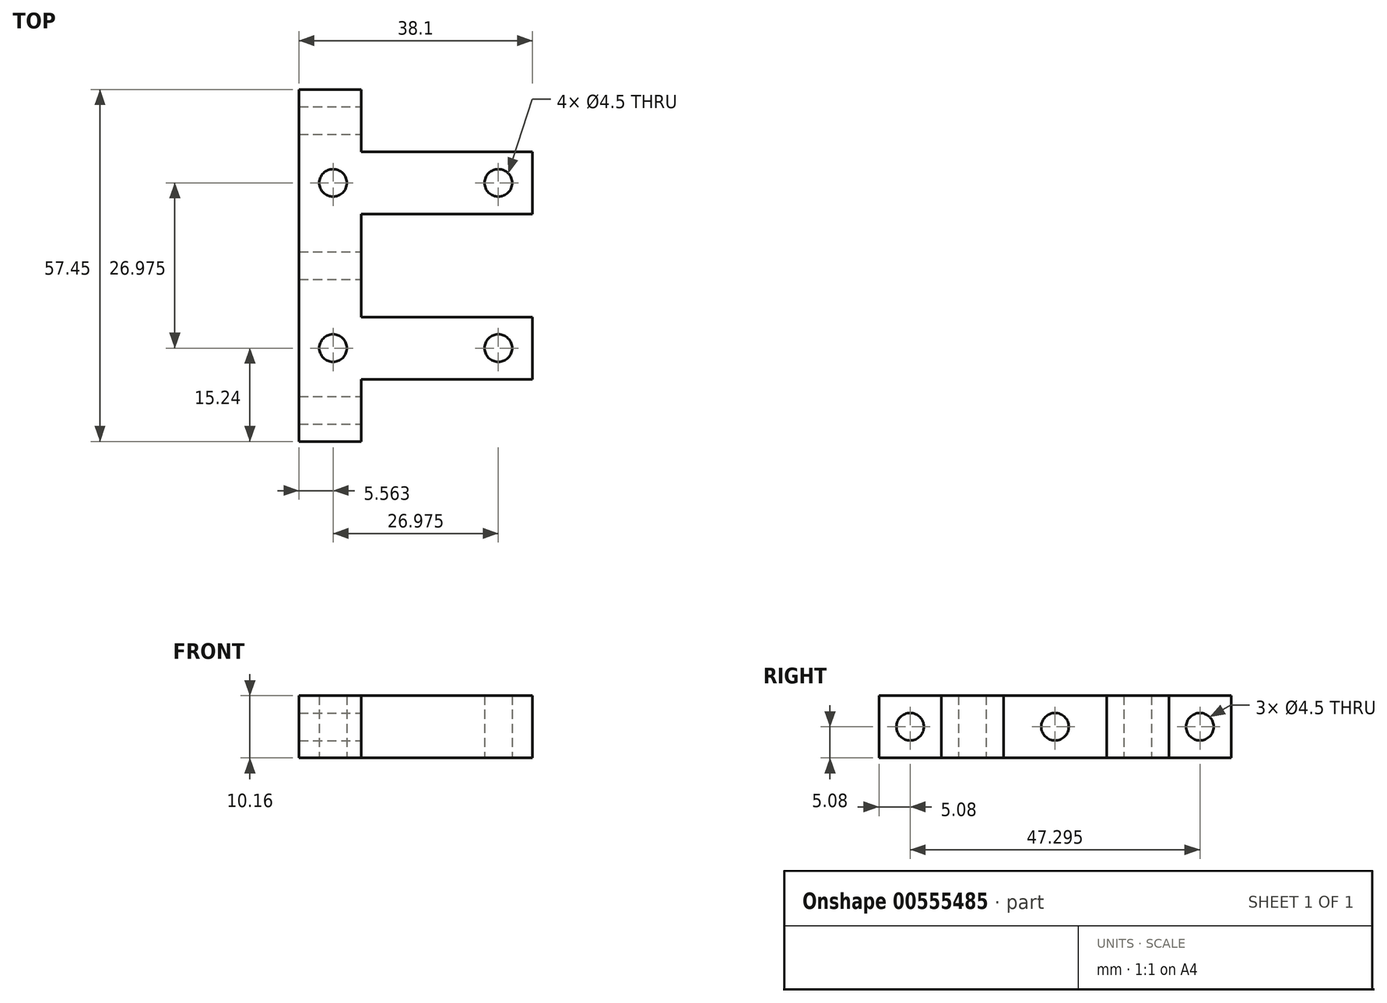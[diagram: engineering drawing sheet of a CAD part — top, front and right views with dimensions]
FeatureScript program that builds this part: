
annotation { "Feature Type Name" : "Feature", "Feature Type Description" : "" }
export const myFeature = defineFeature(function(context is Context, id is Id, definition is map)
    precondition{}
    {
        {
            var Q0;
            Q0=qCreatedBy(makeId("Top.planeOp"),FACE);
            var sketch = newSketch(context, id + "F0", { "sketchPlane" : qUnion([Q0])});
            skLineSegment(sketch, "E0.top", {"start": v(-19.05, -5.08) * mm, "end": v(19.05, -5.08) * mm});
            skPoint(sketch, "E0.middle", {"position": v(0, 0) * mm});
            skLineSegment(sketch, "E1", {"start": v(0, -30.1) * mm, "end": v(0, 45.98) * mm, "construction": true});
            skPoint(sketch, "E2", {"position": v(0, -5.08) * mm});
            skLineSegment(sketch, "E3", {"start": v(19.05, -5.08) * mm, "end": v(19.05, 5.08) * mm});
            skPoint(sketch, "E4", {"position": v(19.05, 0) * mm});
            skLineSegment(sketch, "E5", {"start": v(19.05, 0) * mm, "end": v(-19.05, 0) * mm, "construction": true});
            skPoint(sketch, "E6", {"position": v(-13.49, 0) * mm});
            skPoint(sketch, "E7", {"position": v(13.49, 0) * mm});
            skLineSegment(sketch, "E8", {"start": v(-19.05, -5.08) * mm, "end": v(-19.05, 32.05) * mm});
            skLineSegment(sketch, "E9", {"start": v(19.05, 5.08) * mm, "end": v(-8.89, 5.08) * mm});
            skLineSegment(sketch, "E10", {"start": v(-13.49, -5.08) * mm, "end": v(-13.49, 32.61) * mm, "construction": true});
            skPoint(sketch, "E11", {"position": v(-13.49, 26.97) * mm});
            skLineSegment(sketch, "E12", {"start": v(-19.05, 32.05) * mm, "end": v(19.05, 32.05) * mm});
            skLineSegment(sketch, "E13", {"start": v(-13.49, 26.97) * mm, "end": v(18.99, 26.97) * mm, "construction": true});
            skLineSegment(sketch, "E14", {"start": v(19.05, 32.05) * mm, "end": v(19.05, 21.9) * mm});
            skLineSegment(sketch, "E15", {"start": v(19.05, 21.9) * mm, "end": v(-8.9, 21.9) * mm});
            skLineSegment(sketch, "E16", {"start": v(-8.9, 21.9) * mm, "end": v(-8.89, 5.08) * mm});
            skPoint(sketch, "E17", {"position": v(13.49, 26.97) * mm});
            skLineSegment(sketch, "E18", {"start": v(-8.89, 5.08) * mm, "end": v(-8.89, -15.24) * mm});
            skLineSegment(sketch, "E19", {"start": v(-8.89, -15.24) * mm, "end": v(-19.05, -15.24) * mm});
            skLineSegment(sketch, "E20", {"start": v(-19.05, -15.24) * mm, "end": v(-19.05, -5.08) * mm});
            skLineSegment(sketch, "E21", {"start": v(-8.9, 21.9) * mm, "end": v(-8.9, 42.21) * mm});
            skLineSegment(sketch, "E22", {"start": v(-8.9, 42.21) * mm, "end": v(-19.05, 42.21) * mm});
            skLineSegment(sketch, "E23", {"start": v(-19.05, 42.21) * mm, "end": v(-19.05, 32.05) * mm});
            skSolve(sketch);
        }
        {
            var Q0;
            Q0 = qSketchRegion(id + "F0", true);
            extrude(context, id + "F1", {"entities" : qUnion([Q0]), "depth" : 10.16 * mm, "offsetDistance" : 25.4 * mm});
        }
        {
            var Q0;
            Q0=sQuery(id+"F0.wireOp",VERTEX,"3a61d8f7-f8bc-4dec-a944-f5aff6b2b3ac");
            var Q1;
            Q1=sQuery(id+"F0.wireOp",VERTEX,"E7");
            var Q2;
            Q2=makeQuery(id+"F1.opExtrude","SWEPT_BODY",BODY,{"disambiguationData":[OSD([sQuery(id+"F0.wireOp",EDGE,"E0.top"),sQuery(id+"F0.wireOp",EDGE,"E0.left"),sQuery(id+"F0.wireOp",EDGE,"E0.right"),sQuery(id+"F0.wireOp",EDGE,"jGi3rCr7-3a02-cwpx-b8UE-5agAnS6ffEaF"),sQuery(id+"F0.wireOp",EDGE,"PWNL4rhi-3Qp7-rYPj-jEMt-dBg0OLWIf8hG"),sQuery(id+"F0.wireOp",EDGE,"Bpgq8YRX-R5gd-kBSt-c8g7-r7VuFiH7yYXC"),sQuery(id+"F0.wireOp",EDGE,"3xZXgOuL-xQpx-ldTr-aVNf-GDxRYF5nVHXa"),sQuery(id+"F0.wireOp",EDGE,"6zk2t0zq-t04g-zjlz-O0ZE-NBeQm2xF9ogC"),sQuery(id+"F0.wireOp",EDGE,"IcurCVpb-tRY3-wefo-Cpvh-wi3rbwIS9VJQ")])]});
            hole(context, id + "F2", {"style" : HoleStyle.SIMPLE, "endStyle" : HoleEndStyle.THROUGH, "oppositeDirection" : true, "standardTappedOrClearance" : lookupTablePath({ "standard" : "ANSI", "fit" : "Normal (ASME)", "size" : "#8", "type" : "Clearance" }), "standardBlindInLast" : lookupTablePath({ "fit" : "Free", "standard" : "ANSI", "size" : "#8", "type" : "Clearance" }), "holeDiameter" : 4.5 * mm, "isTappedThrough" : true, "tappedDepth" : 12.7 * mm, "tapClearance" : 3, "locations" : qUnion([Q0, Q1]), "scope" : qUnion([Q2])});
        }
        {
            var Q0;
            Q0=sQuery(id+"F0.wireOp",VERTEX,"c50f6436-d472-4689-83e9-5a35b1037d48");
            var Q1;
            Q1=sQuery(id+"F0.wireOp",VERTEX,"E6");
            var Q2;
            Q2=makeQuery(id+"F1.opExtrude","SWEPT_BODY",BODY,{"disambiguationData":[OSD([sQuery(id+"F0.wireOp",EDGE,"E0.top"),sQuery(id+"F0.wireOp",EDGE,"E0.left"),sQuery(id+"F0.wireOp",EDGE,"E0.right"),sQuery(id+"F0.wireOp",EDGE,"jGi3rCr7-3a02-cwpx-b8UE-5agAnS6ffEaF"),sQuery(id+"F0.wireOp",EDGE,"PWNL4rhi-3Qp7-rYPj-jEMt-dBg0OLWIf8hG"),sQuery(id+"F0.wireOp",EDGE,"Bpgq8YRX-R5gd-kBSt-c8g7-r7VuFiH7yYXC"),sQuery(id+"F0.wireOp",EDGE,"3xZXgOuL-xQpx-ldTr-aVNf-GDxRYF5nVHXa"),sQuery(id+"F0.wireOp",EDGE,"6zk2t0zq-t04g-zjlz-O0ZE-NBeQm2xF9ogC"),sQuery(id+"F0.wireOp",EDGE,"IcurCVpb-tRY3-wefo-Cpvh-wi3rbwIS9VJQ")])]});
            hole(context, id + "F3", {"style" : HoleStyle.SIMPLE, "endStyle" : HoleEndStyle.THROUGH, "oppositeDirection" : true, "standardTappedOrClearance" : lookupTablePath({ "standard" : "ANSI", "fit" : "Normal (ASME)", "size" : "#8", "type" : "Clearance" }), "standardBlindInLast" : lookupTablePath({ "fit" : "Free", "standard" : "ANSI", "size" : "#8", "type" : "Clearance" }), "holeDiameter" : 4.5 * mm, "isTappedThrough" : true, "tappedDepth" : 12.7 * mm, "tapClearance" : 3, "locations" : qUnion([Q0, Q1]), "scope" : qUnion([Q2])});
        }
        {
            var Q0;
            Q0=sQuery(id+"F0.wireOp",VERTEX,"d58ae2e4-0c6b-4f90-ab22-40fbd0efa159");
            var Q1;
            Q1=sQuery(id+"F0.wireOp",VERTEX,"E11");
            var Q2;
            Q2=makeQuery(id+"F1.opExtrude","SWEPT_BODY",BODY,{"disambiguationData":[OSD([sQuery(id+"F0.wireOp",EDGE,"E0.top"),sQuery(id+"F0.wireOp",EDGE,"E0.left"),sQuery(id+"F0.wireOp",EDGE,"E0.right"),sQuery(id+"F0.wireOp",EDGE,"jGi3rCr7-3a02-cwpx-b8UE-5agAnS6ffEaF"),sQuery(id+"F0.wireOp",EDGE,"PWNL4rhi-3Qp7-rYPj-jEMt-dBg0OLWIf8hG"),sQuery(id+"F0.wireOp",EDGE,"Bpgq8YRX-R5gd-kBSt-c8g7-r7VuFiH7yYXC"),sQuery(id+"F0.wireOp",EDGE,"3xZXgOuL-xQpx-ldTr-aVNf-GDxRYF5nVHXa"),sQuery(id+"F0.wireOp",EDGE,"6zk2t0zq-t04g-zjlz-O0ZE-NBeQm2xF9ogC"),sQuery(id+"F0.wireOp",EDGE,"IcurCVpb-tRY3-wefo-Cpvh-wi3rbwIS9VJQ")])]});
            hole(context, id + "F4", {"style" : HoleStyle.SIMPLE, "endStyle" : HoleEndStyle.THROUGH, "oppositeDirection" : true, "standardTappedOrClearance" : lookupTablePath({ "standard" : "ANSI", "fit" : "Normal (ASME)", "size" : "#8", "type" : "Clearance" }), "standardBlindInLast" : lookupTablePath({ "fit" : "Free", "standard" : "ANSI", "size" : "#8", "type" : "Clearance" }), "holeDiameter" : 4.5 * mm, "isTappedThrough" : true, "tappedDepth" : 12.7 * mm, "tapClearance" : 3, "locations" : qUnion([Q0, Q1]), "scope" : qUnion([Q2])});
        }
        {
            var Q0;
            Q0=sQuery(id+"F0.wireOp",VERTEX,"684fd054-121e-4c5f-bf13-0b8425f3b707");
            var Q1;
            Q1=sQuery(id+"F0.wireOp",VERTEX,"E17");
            var Q2;
            Q2=makeQuery(id+"F1.opExtrude","SWEPT_BODY",BODY,{"disambiguationData":[OSD([sQuery(id+"F0.wireOp",EDGE,"E0.top"),sQuery(id+"F0.wireOp",EDGE,"E0.left"),sQuery(id+"F0.wireOp",EDGE,"E0.right"),sQuery(id+"F0.wireOp",EDGE,"jGi3rCr7-3a02-cwpx-b8UE-5agAnS6ffEaF"),sQuery(id+"F0.wireOp",EDGE,"PWNL4rhi-3Qp7-rYPj-jEMt-dBg0OLWIf8hG"),sQuery(id+"F0.wireOp",EDGE,"Bpgq8YRX-R5gd-kBSt-c8g7-r7VuFiH7yYXC"),sQuery(id+"F0.wireOp",EDGE,"3xZXgOuL-xQpx-ldTr-aVNf-GDxRYF5nVHXa"),sQuery(id+"F0.wireOp",EDGE,"6zk2t0zq-t04g-zjlz-O0ZE-NBeQm2xF9ogC"),sQuery(id+"F0.wireOp",EDGE,"IcurCVpb-tRY3-wefo-Cpvh-wi3rbwIS9VJQ")])]});
            hole(context, id + "F5", {"style" : HoleStyle.SIMPLE, "endStyle" : HoleEndStyle.THROUGH, "oppositeDirection" : true, "standardTappedOrClearance" : lookupTablePath({ "standard" : "ANSI", "fit" : "Normal (ASME)", "size" : "#8", "type" : "Clearance" }), "standardBlindInLast" : lookupTablePath({ "fit" : "Free", "standard" : "ANSI", "size" : "#8", "type" : "Clearance" }), "holeDiameter" : 4.5 * mm, "isTappedThrough" : true, "tappedDepth" : 12.7 * mm, "tapClearance" : 3, "locations" : qUnion([Q0, Q1]), "scope" : qUnion([Q2])});
        }
        {
            var Q0;
            Q0=makeQuery(id+"F1.opExtrude","SWEPT_FACE",FACE,{"disambiguationData":[OSD([sQuery(id+"F0.wireOp",EDGE,"E16")])]});
            var sketch = newSketch(context, id + "F6", { "sketchPlane" : qUnion([Q0])});
            skPoint(sketch, "E24", {"position": v(13.49, 5.08) * mm});
            skSolve(sketch);
        }
        {
            var Q0;
            Q0=sQuery(id+"F6.wireOp",VERTEX,"09b015fe-b464-462a-a877-3ab7e384d40e");
            var Q1;
            Q1=sQuery(id+"F6.wireOp",VERTEX,"E24");
            var Q2;
            Q2=makeQuery(id+"F1.opExtrude","SWEPT_BODY",BODY,{"disambiguationData":[OSD([sQuery(id+"F0.wireOp",EDGE,"E0.top"),sQuery(id+"F0.wireOp",EDGE,"E3"),sQuery(id+"F0.wireOp",EDGE,"E8"),sQuery(id+"F0.wireOp",EDGE,"E9"),sQuery(id+"F0.wireOp",EDGE,"E12"),sQuery(id+"F0.wireOp",EDGE,"E14"),sQuery(id+"F0.wireOp",EDGE,"E15"),sQuery(id+"F0.wireOp",EDGE,"E16")])]});
            hole(context, id + "F7", {"style" : HoleStyle.SIMPLE, "endStyle" : HoleEndStyle.THROUGH, "standardTappedOrClearance" : lookupTablePath({ "standard" : "ANSI", "fit" : "Normal (ASME)", "size" : "#8", "type" : "Clearance" }), "standardBlindInLast" : lookupTablePath({ "fit" : "Free", "standard" : "ANSI", "size" : "#8", "type" : "Clearance" }), "holeDiameter" : 4.5 * mm, "isTappedThrough" : true, "tappedDepth" : 12.7 * mm, "tapClearance" : 3, "locations" : qUnion([Q0, Q1]), "scope" : qUnion([Q2])});
        }
        {
            var Q0;
            Q0=makeQuery(id+"F1.opExtrude","SWEPT_FACE",FACE,{"disambiguationData":[OSD([sQuery(id+"F0.wireOp",EDGE,"E18")])]});
            var sketch = newSketch(context, id + "F8", { "sketchPlane" : qUnion([Q0])});
            skLineSegment(sketch, "E25", {"start": v(-15.24, 5.08) * mm, "end": v(-5.08, 5.08) * mm, "construction": true});
            skPoint(sketch, "E26", {"position": v(-10.16, 5.08) * mm});
            skSolve(sketch);
        }
        {
            var Q0;
            Q0=makeQuery(id+"F1.opExtrude","SWEPT_FACE",FACE,{"disambiguationData":[OSD([sQuery(id+"F0.wireOp",EDGE,"E21")])]});
            var sketch = newSketch(context, id + "F9", { "sketchPlane" : qUnion([Q0])});
            skLineSegment(sketch, "E27", {"start": v(32.05, 5.08) * mm, "end": v(42.21, 5.08) * mm, "construction": true});
            skPoint(sketch, "E28", {"position": v(37.13, 5.08) * mm});
            skSolve(sketch);
        }
        {
            var Q0;
            Q0=sQuery(id+"F8.wireOp",VERTEX,"E26");
            var Q1;
            Q1=makeQuery(id+"F1.opExtrude","SWEPT_BODY",BODY,{"disambiguationData":[OSD([sQuery(id+"F0.wireOp",EDGE,"E0.top"),sQuery(id+"F0.wireOp",EDGE,"E3"),sQuery(id+"F0.wireOp",EDGE,"E8"),sQuery(id+"F0.wireOp",EDGE,"E9"),sQuery(id+"F0.wireOp",EDGE,"E12"),sQuery(id+"F0.wireOp",EDGE,"E14"),sQuery(id+"F0.wireOp",EDGE,"E15"),sQuery(id+"F0.wireOp",EDGE,"E16"),sQuery(id+"F0.wireOp",EDGE,"E18"),sQuery(id+"F0.wireOp",EDGE,"E19"),sQuery(id+"F0.wireOp",EDGE,"E20"),sQuery(id+"F0.wireOp",EDGE,"E21"),sQuery(id+"F0.wireOp",EDGE,"E22"),sQuery(id+"F0.wireOp",EDGE,"E23")])]});
            hole(context, id + "F10", {"style" : HoleStyle.SIMPLE, "endStyle" : HoleEndStyle.THROUGH, "standardTappedOrClearance" : lookupTablePath({ "standard" : "ANSI", "fit" : "Normal (ASME)", "size" : "#8", "type" : "Clearance" }), "standardBlindInLast" : lookupTablePath({ "fit" : "Free", "standard" : "ANSI", "size" : "#8", "type" : "Clearance" }), "holeDiameter" : 4.5 * mm, "isTappedThrough" : true, "tappedDepth" : 12.7 * mm, "tapClearance" : 3, "locations" : qUnion([Q0]), "scope" : qUnion([Q1])});
        }
        {
            var Q0;
            Q0=sQuery(id+"F9.wireOp",VERTEX,"E28");
            var Q1;
            Q1=makeQuery(id+"F1.opExtrude","SWEPT_BODY",BODY,{"disambiguationData":[OSD([sQuery(id+"F0.wireOp",EDGE,"E0.top"),sQuery(id+"F0.wireOp",EDGE,"E3"),sQuery(id+"F0.wireOp",EDGE,"E8"),sQuery(id+"F0.wireOp",EDGE,"E9"),sQuery(id+"F0.wireOp",EDGE,"E12"),sQuery(id+"F0.wireOp",EDGE,"E14"),sQuery(id+"F0.wireOp",EDGE,"E15"),sQuery(id+"F0.wireOp",EDGE,"E16"),sQuery(id+"F0.wireOp",EDGE,"E18"),sQuery(id+"F0.wireOp",EDGE,"E19"),sQuery(id+"F0.wireOp",EDGE,"E20"),sQuery(id+"F0.wireOp",EDGE,"E21"),sQuery(id+"F0.wireOp",EDGE,"E22"),sQuery(id+"F0.wireOp",EDGE,"E23")])]});
            hole(context, id + "F11", {"style" : HoleStyle.SIMPLE, "endStyle" : HoleEndStyle.THROUGH, "standardTappedOrClearance" : lookupTablePath({ "standard" : "ANSI", "fit" : "Normal (ASME)", "size" : "#8", "type" : "Clearance" }), "standardBlindInLast" : lookupTablePath({ "fit" : "Free", "standard" : "ANSI", "size" : "#8", "type" : "Clearance" }), "holeDiameter" : 4.5 * mm, "isTappedThrough" : true, "tappedDepth" : 12.7 * mm, "tapClearance" : 3, "locations" : qUnion([Q0]), "scope" : qUnion([Q1])});
        }
    });
